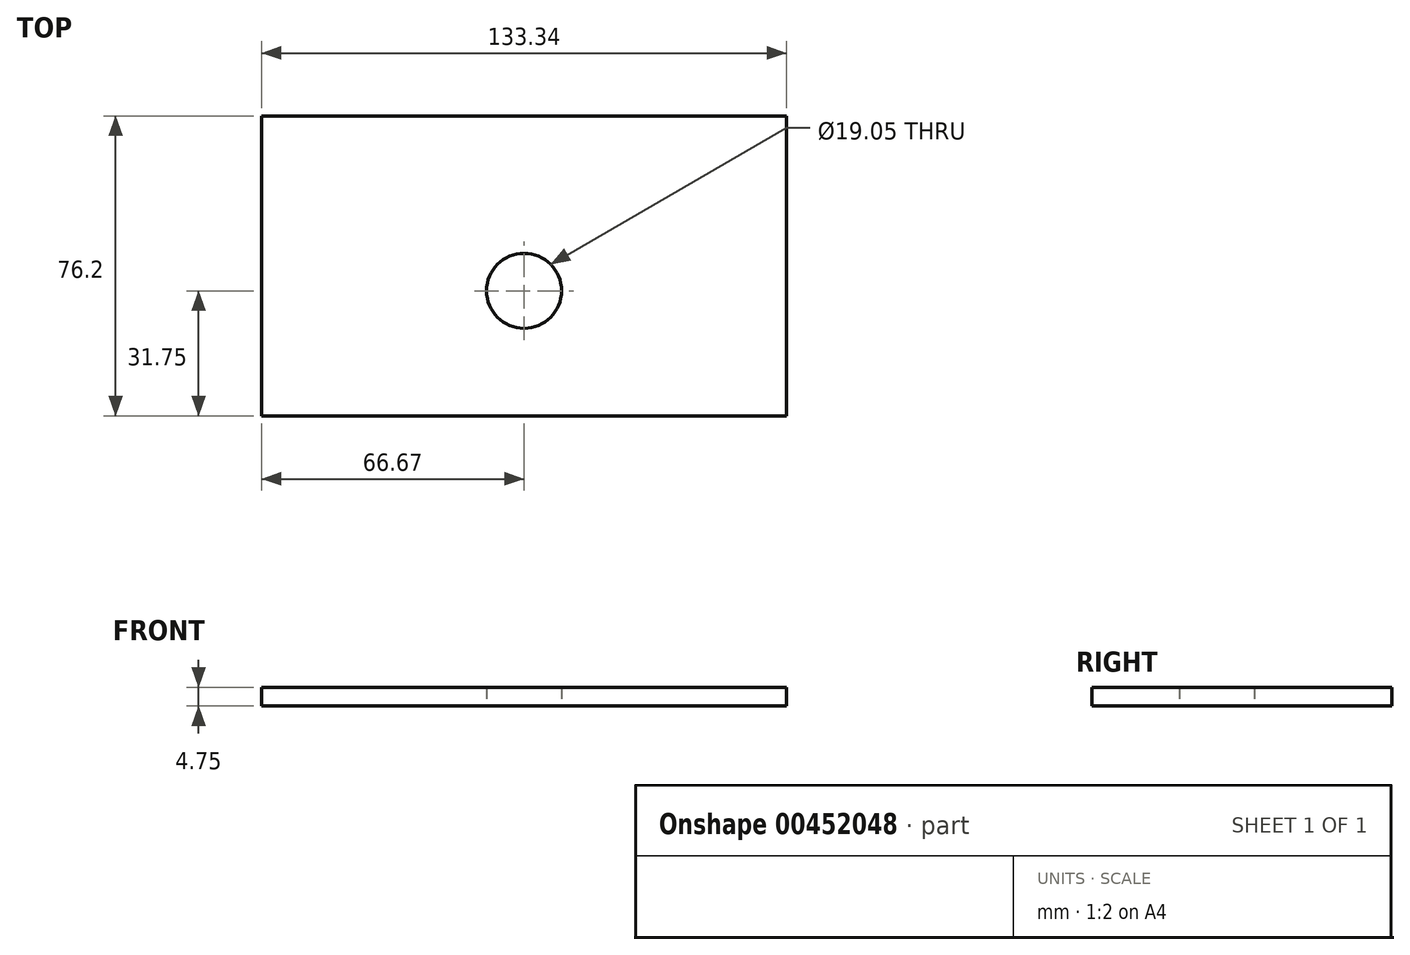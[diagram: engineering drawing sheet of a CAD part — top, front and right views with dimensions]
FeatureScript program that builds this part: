
annotation { "Feature Type Name" : "Feature", "Feature Type Description" : "" }
export const myFeature = defineFeature(function(context is Context, id is Id, definition is map)
    precondition{}
    {
        {
            var Q0;
            Q0=qCreatedBy(makeId("Top.planeOp"),FACE);
            var sketch = newSketch(context, id + "F0", { "sketchPlane" : qUnion([Q0])});
            skLineSegment(sketch, "E0.bottom", {"start": v(66.68, -38.1) * mm, "end": v(-66.68, -38.1) * mm});
            skLineSegment(sketch, "E0.top", {"start": v(66.68, 38.1) * mm, "end": v(-66.68, 38.1) * mm});
            skLineSegment(sketch, "E0.left", {"start": v(66.68, -38.1) * mm, "end": v(66.68, 38.1) * mm});
            skLineSegment(sketch, "E0.right", {"start": v(-66.68, -38.1) * mm, "end": v(-66.68, 38.1) * mm});
            skPoint(sketch, "E0.middle", {"position": v(0, 0) * mm});
            skCircle(sketch, "E1", {"center": v(0, -6.35) * mm, "radius": 9.53 * mm});
            skSolve(sketch);
        }
        {
            var Q0;
            Q0=makeQuery(id+"F0.imprint","IMPRINT",FACE,{"disambiguationData":[TD([[makeQuery(id+"F0.imprint","IMPRINT",EDGE,{"derivedFrom":sQuery(id+"F0.wireOp",EDGE,"E0.bottom")}),-1.0]])]});
            extrude(context, id + "F1", {"entities" : qUnion([Q0]), "depth" : 4.75 * mm});
        }
    });
